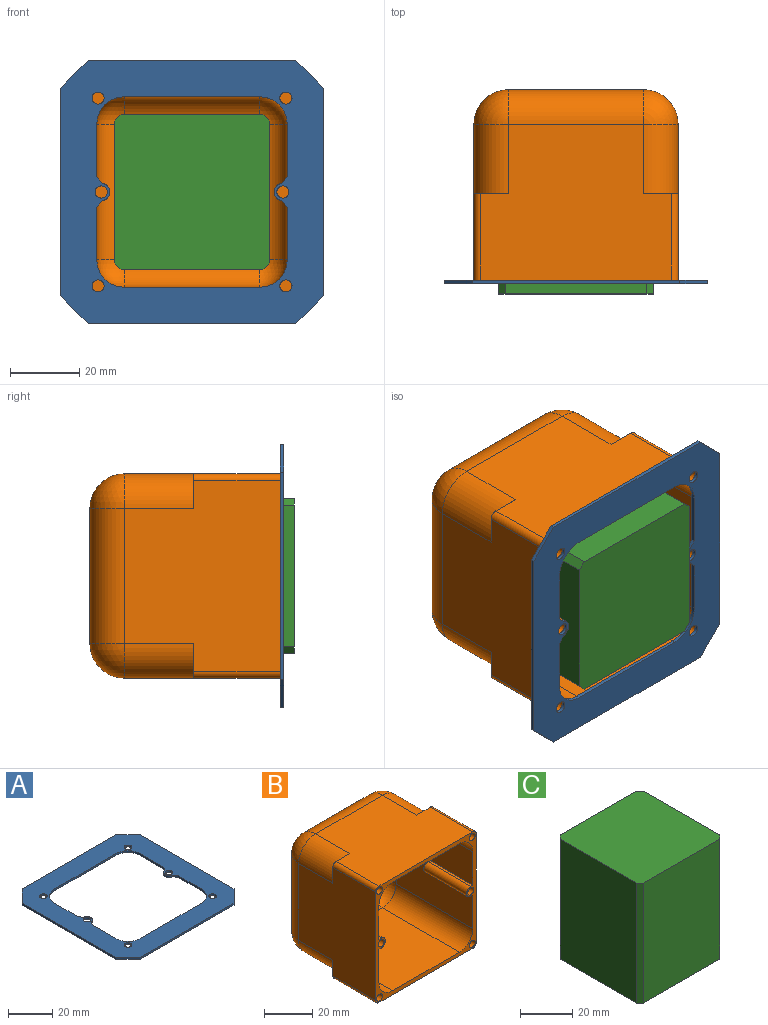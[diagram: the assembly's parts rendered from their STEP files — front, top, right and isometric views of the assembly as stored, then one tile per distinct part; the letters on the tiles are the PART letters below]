
ASSEMBLY  parts=3 mates=1
PART A: 32 faces, bbox 76x76x1 mm
  f0: plane 15.06x1mm, normal (1,0,0), area 15.1mm2, adj f1,f18,f19,f30
  f1: cylinder r=8mm len=8mm, axis (0,0,-1), area 12.6mm2, adj f0,f2,f18,f19
  f2: plane 39x1mm, normal (0,-1,0), area 39mm2, adj f1,f3,f18,f19
  f3: cylinder r=8mm len=8mm, axis (0,0,-1), area 12.6mm2, adj f2,f4,f18,f19
  f4: plane 15.06x1mm, normal (-1,0,0), area 15.1mm2, adj f3,f18,f19,f28
  f5: cylinder r=2.5mm len=4.93mm, axis (0,0,-1), area 7mm2, adj f18,f19,f28,f29
  f6: plane 15.06x1mm, normal (-1,0,0), area 15.1mm2, adj f7,f18,f19,f29
  f7: cylinder r=8mm len=8mm, axis (0,0,-1), area 12.6mm2, adj f6,f8,f18,f19
  f8: plane 39x1mm, normal (0,1,0), area 39mm2, adj f7,f9,f18,f19
  f9: cylinder r=8mm len=8mm, axis (0,0,-1), area 12.6mm2, adj f8,f10,f18,f19
  f10: plane 15.06x1mm, normal (1,0,0), area 15.1mm2, adj f9,f18,f19,f31
  f11: cylinder r=1.75mm len=3.5mm, axis (0,0,-1), area 11mm2, adj f18,f19
  f12: cylinder r=1.75mm len=3.5mm, axis (0,0,-1), area 11mm2, adj f18,f19
  f13: cylinder r=1.75mm len=3.5mm, axis (0,0,-1), area 11mm2, adj f18,f19
  f14: cylinder r=1.75mm len=3.5mm, axis (0,0,-1), area 11mm2, adj f18,f19
  f15: cylinder r=1.75mm len=3.5mm, axis (0,0,-1), area 11mm2, adj f18,f19
  f16: cylinder r=1.75mm len=3.5mm, axis (0,0,-1), area 11mm2, adj f18,f19
  f17: cylinder r=2.5mm len=4.93mm, axis (0,0,-1), area 7mm2, adj f18,f19,f30,f31
  f18: plane 76x76mm, normal (0,0,1), area 2658.7mm2, adj f0,f1,f2,f3,f4,f5,f6,f7
  f19: plane 76x76mm, normal (0,0,-1), area 2658.7mm2, adj f0,f1,f2,f3,f4,f5,f6,f7
  f20: plane 60x1mm, normal (0,1,0), area 60mm2, adj f18,f19,f24,f25
  f21: plane 60x1mm, normal (-1,0,0), area 60mm2, adj f18,f19,f24,f27
  f22: plane 60x1mm, normal (1,0,0), area 60mm2, adj f18,f19,f25,f26
  f23: plane 60x1mm, normal (0,-1,0), area 60mm2, adj f18,f19,f26,f27
  f24: plane 8x8mm, normal (-0.71,0.71,0), area 11.3mm2, adj f18,f19,f20,f21
  f25: plane 8x8mm, normal (0.71,0.71,0), area 11.3mm2, adj f18,f19,f20,f22
  f26: plane 8x8mm, normal (0.71,-0.71,0), area 11.3mm2, adj f18,f19,f22,f23
  f27: plane 8x8mm, normal (-0.71,-0.71,0), area 11.3mm2, adj f18,f19,f21,f23
  f28: plane 1.97x1.67mm, normal (-0.76,0.65,0), area 2.6mm2, adj f4,f5,f18,f19
  f29: plane 1.97x1.67mm, normal (-0.76,-0.65,0), area 2.6mm2, adj f5,f6,f18,f19
  f30: plane 1.97x1.67mm, normal (0.76,0.65,0), area 2.6mm2, adj f0,f17,f18,f19
  f31: plane 1.97x1.67mm, normal (0.76,-0.65,0), area 2.6mm2, adj f10,f17,f18,f19
PART B: 63 faces, bbox 59x55x59 mm
  f0: plane 59x59mm, normal (0,-1,0), area 481.9mm2, adj f1,f2,f3,f4,f5,f19,f20,f21
  f1: plane 45x39mm, normal (1,0,0), area 1630mm2, adj f0,f23,f27,f28,f40,f41,f42
  f2: plane 55x45mm, normal (0,0,-1), area 2155mm2, adj f0,f12,f16,f18,f37,f38,f59,f60
  f3: plane 55x45mm, normal (1,0,0), area 2155mm2, adj f0,f9,f15,f18,f35,f38,f59,f62
  f4: plane 55x45mm, normal (0,0,1), area 2155mm2, adj f0,f7,f9,f10,f35,f36,f61,f62
  f5: plane 55x45mm, normal (-1,0,0), area 2155mm2, adj f0,f7,f11,f12,f36,f37,f60,f61
  f6: plane 39x39mm, normal (0,1,0), area 1521mm2, adj f10,f11,f15,f16
  f7: cylinder r=10mm len=20mm, axis (0,-1,0), area 314.2mm2, adj f4,f5,f8,f36
  f8: sphere r=10mm, area 157.1mm2, adj f7,f10,f11
  f9: cylinder r=10mm len=20mm, axis (0,1,0), area 314.2mm2, adj f3,f4,f13,f35
  f10: cylinder r=10mm len=39mm, axis (-1,0,0), area 612.6mm2, adj f4,f6,f8,f13
  f11: cylinder r=10mm len=39mm, axis (0,0,-1), area 612.6mm2, adj f5,f6,f8,f14
  f12: cylinder r=10mm len=20mm, axis (0,1,0), area 314.2mm2, adj f2,f5,f14,f37
  f13: sphere r=10mm, area 157.1mm2, adj f9,f10,f15
  f14: sphere r=10mm, area 157.1mm2, adj f11,f12,f16
  f15: cylinder r=10mm len=39mm, axis (0,0,1), area 612.6mm2, adj f3,f6,f13,f17
  f16: cylinder r=10mm len=39mm, axis (1,0,0), area 612.6mm2, adj f2,f6,f14,f17
  f17: sphere r=10mm, area 157.1mm2, adj f15,f16,f18
  f18: cylinder r=10mm len=20mm, axis (0,-1,0), area 314.2mm2, adj f2,f3,f17,f38
  f19: plane 45x39mm, normal (0,0,1), area 1755mm2, adj f0,f28,f32,f34
  f20: plane 45x39mm, normal (-1,0,0), area 1630mm2, adj f0,f25,f31,f34,f43,f45,f46
  f21: plane 45x39mm, normal (0,0,-1), area 1755mm2, adj f0,f23,f25,f26
  f22: plane 39x39mm, normal (0,-1,0), area 1521mm2, adj f26,f27,f31,f32
  f23: cylinder r=8mm len=45mm, axis (0,-1,0), area 565.5mm2, adj f0,f1,f21,f24
  f24: sphere r=8mm, area 100.5mm2, adj f23,f26,f27
  f25: cylinder r=8mm len=45mm, axis (0,1,0), area 565.5mm2, adj f0,f20,f21,f29
  f26: cylinder r=8mm len=39mm, axis (-1,0,0), area 490.1mm2, adj f21,f22,f24,f29
  f27: cylinder r=8mm len=39mm, axis (0,0,-1), area 490.1mm2, adj f1,f22,f24,f30
  f28: cylinder r=8mm len=45mm, axis (0,1,0), area 565.5mm2, adj f0,f1,f19,f30
  f29: sphere r=8mm, area 100.5mm2, adj f25,f26,f31
  f30: sphere r=8mm, area 100.5mm2, adj f27,f28,f32
  f31: cylinder r=8mm len=39mm, axis (0,0,1), area 490.1mm2, adj f20,f22,f29,f33
  f32: cylinder r=8mm len=39mm, axis (1,0,0), area 490.1mm2, adj f19,f22,f30,f33
  f33: sphere r=8mm, area 100.5mm2, adj f31,f32,f34
  f34: cylinder r=8mm len=45mm, axis (0,-1,0), area 565.5mm2, adj f0,f19,f20,f33
  f35: plane 10x10mm, normal (0,1,0), area 20.6mm2, adj f3,f4,f9,f62
  f36: plane 10x10mm, normal (0,1,0), area 20.6mm2, adj f4,f5,f7,f61
  f37: plane 10x10mm, normal (0,1,0), area 20.6mm2, adj f2,f5,f12,f60
  f38: plane 10x10mm, normal (0,1,0), area 20.6mm2, adj f2,f3,f18,f59
  f39: cylinder r=2.5mm len=25mm, axis (0,-1,0), area 196.3mm2, adj f0,f40,f41,f42
  f40: plane 25x1.25mm, normal (0,0,1), area 31.3mm2, adj f0,f1,f39,f42
  f41: plane 25x1.25mm, normal (0,0,-1), area 31.3mm2, adj f0,f1,f39,f42
  f42: plane 5x3.75mm, normal (0,1,0), area 16.1mm2, adj f1,f39,f40,f41
  f43: plane 25x1.25mm, normal (0,0,1), area 31.3mm2, adj f0,f20,f44,f46
  f44: cylinder r=2.5mm len=25mm, axis (0,-1,0), area 196.3mm2, adj f0,f43,f45,f46
  f45: plane 25x1.25mm, normal (0,0,-1), area 31.3mm2, adj f0,f20,f44,f46
  f46: plane 5x3.75mm, normal (0,1,0), area 16.1mm2, adj f20,f43,f44,f45
  f47: cylinder r=1.75mm len=20mm, axis (0,-1,0), area 219.9mm2, adj f0,f48
  f48: plane 3.5x3.5mm, normal (0,-1,0), area 9.6mm2, adj f47
  f49: cylinder r=1.75mm len=20mm, axis (0,-1,0), area 219.9mm2, adj f0,f50
  f50: plane 3.5x3.5mm, normal (0,-1,0), area 9.6mm2, adj f49
  f51: cylinder r=1.75mm len=20mm, axis (0,-1,0), area 219.9mm2, adj f0,f52
  f52: plane 3.5x3.5mm, normal (0,-1,0), area 9.6mm2, adj f51
  f53: cylinder r=1.75mm len=20mm, axis (0,-1,0), area 219.9mm2, adj f0,f54
  f54: plane 3.5x3.5mm, normal (0,-1,0), area 9.6mm2, adj f53
  f55: cylinder r=1.75mm len=20mm, axis (0,-1,0), area 219.9mm2, adj f0,f56
  f56: plane 3.5x3.5mm, normal (0,-1,0), area 9.6mm2, adj f55
  f57: cylinder r=1.75mm len=20mm, axis (0,-1,0), area 219.9mm2, adj f0,f58
  f58: plane 3.5x3.5mm, normal (0,-1,0), area 9.6mm2, adj f57
  f59: cylinder r=2mm len=25mm, axis (0,1,0), area 78.5mm2, adj f0,f2,f3,f38
  f60: cylinder r=2mm len=25mm, axis (0,-1,0), area 78.5mm2, adj f0,f2,f5,f37
  f61: cylinder r=2mm len=25mm, axis (0,1,0), area 78.5mm2, adj f0,f4,f5,f36
  f62: cylinder r=2mm len=25mm, axis (0,-1,0), area 78.5mm2, adj f0,f3,f4,f35
PART C: 10 faces, bbox 45x45x56 mm
  f0: plane 56x41mm, normal (1,0,0), area 2296mm2, adj f4,f5,f7,f8
  f1: plane 56x41mm, normal (0,1,0), area 2296mm2, adj f4,f5,f8,f9
  f2: plane 56x41mm, normal (-1,0,0), area 2296mm2, adj f4,f5,f6,f9
  f3: plane 56x41mm, normal (0,-1,0), area 2296mm2, adj f4,f5,f6,f7
  f4: plane 45x45mm, normal (0,0,-1), area 2017mm2, adj f0,f1,f2,f3,f6,f7,f8,f9
  f5: plane 45x45mm, normal (0,0,1), area 2017mm2, adj f0,f1,f2,f3,f6,f7,f8,f9
  f6: plane 56x2mm, normal (-0.71,-0.71,0), area 158.4mm2, adj f2,f3,f4,f5
  f7: plane 56x2mm, normal (0.71,-0.71,0), area 158.4mm2, adj f0,f3,f4,f5
  f8: plane 56x2mm, normal (0.71,0.71,0), area 158.4mm2, adj f0,f1,f4,f5
  f9: plane 56x2mm, normal (-0.71,0.71,0), area 158.4mm2, adj f1,f2,f4,f5
PLACE A rot(axis=(-1,0,0),90deg) t=(-26.25,-56,0)mm
PLACE B at identity fixed
PLACE C rot(axis=(1,0,0),90deg) t=(0,-55,0)mm
MATE fastened B.f39 <-> A.f12  axis (0,-1,0) through (-26.25,-55,0)mm
